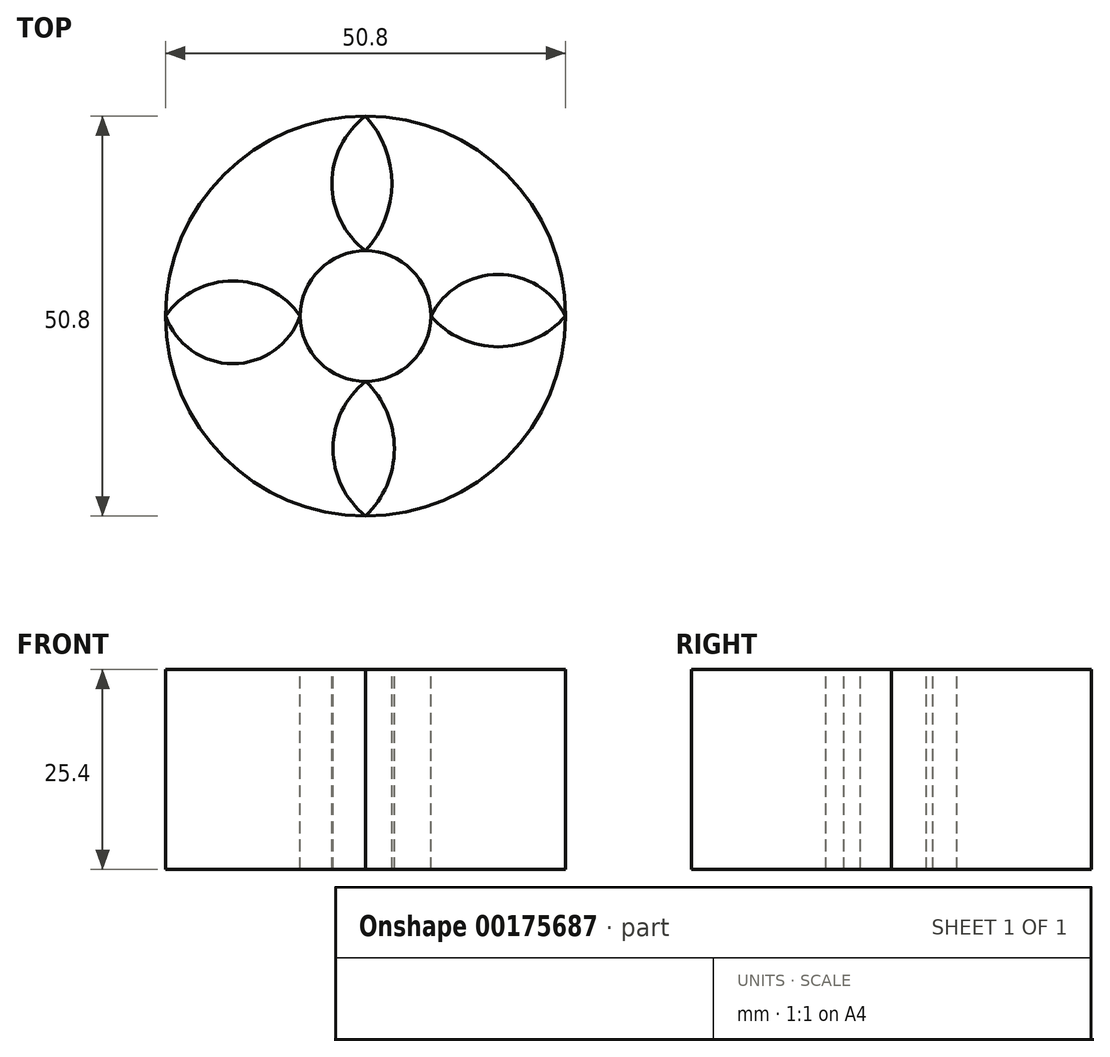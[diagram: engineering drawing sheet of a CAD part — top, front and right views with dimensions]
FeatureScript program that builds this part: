
annotation { "Feature Type Name" : "Feature", "Feature Type Description" : "" }
export const myFeature = defineFeature(function(context is Context, id is Id, definition is map)
    precondition{}
    {
        {
            var Q0;
            Q0=qCreatedBy(makeId("Top.planeOp"),FACE);
            var sketch = newSketch(context, id + "F0", { "sketchPlane" : qUnion([Q0])});
            skCircle(sketch, "E0", {"center": v(0, 0) * mm, "radius": 25.4 * mm});
            skSolve(sketch);
        }
        {
            var Q0;
            Q0 = qSketchRegion(id + "F0", true);
            extrude(context, id + "F1", {"entities" : qUnion([Q0]), "depth" : 25.4 * mm});
        }
        {
            var Q0;
            Q0=makeQuery(id+"F1.opExtrude","CAP_FACE",FACE,{"disambiguationData":[OSD([sQuery(id+"F0.wireOp",EDGE,"E0")])],"isStart":false});
            var sketch = newSketch(context, id + "F2", { "sketchPlane" : qUnion([Q0])});
            skCircle(sketch, "E1", {"center": v(0, 0) * mm, "radius": 8.3 * mm});
            skSolve(sketch);
        }
        {
            var Q0;
            Q0 = qSketchRegion(id + "F2", true);
            extrude(context, id + "F3", {"entities" : qUnion([Q0]), "operationType" : NewBodyOperationType.REMOVE, "endBound" : BoundingType.THROUGH_ALL, "oppositeDirection" : true, "depth" : 25.4 * mm});
        }
        {
            var Q0;
            Q0=makeQuery(id+"F1.opExtrude","CAP_FACE",FACE,{"disambiguationData":[OSD([sQuery(id+"F0.wireOp",EDGE,"E0")])],"isStart":false});
            var sketch = newSketch(context, id + "F4", { "sketchPlane" : qUnion([Q0])});
            skArc(sketch, "E2", {"start": v(0, 25.4) * mm, "mid": v(-4.27, 16.85) * mm, "end": v(0, 8.3) * mm});
            skArc(sketch, "E3", {"start": v(0, 8.3) * mm, "mid": v(3.34, 16.85) * mm, "end": v(0, 25.4) * mm});
            skArc(sketch, "E4", {"start": v(25.4, 0) * mm, "mid": v(16.85, 5.28) * mm, "end": v(8.3, 0) * mm});
            skArc(sketch, "E5", {"start": v(8.3, 0) * mm, "mid": v(16.85, -3.9) * mm, "end": v(25.4, 0) * mm});
            skArc(sketch, "E6", {"start": v(-25.4, 0) * mm, "mid": v(-16.85, -6.06) * mm, "end": v(-8.3, 0) * mm});
            skArc(sketch, "E7", {"start": v(-8.3, 0) * mm, "mid": v(-16.85, 4.46) * mm, "end": v(-25.4, 0) * mm});
            skArc(sketch, "E8", {"start": v(0, -25.4) * mm, "mid": v(3.66, -16.85) * mm, "end": v(0, -8.3) * mm});
            skArc(sketch, "E9", {"start": v(0, -8.3) * mm, "mid": v(-4.12, -16.85) * mm, "end": v(0, -25.4) * mm});
            skSolve(sketch);
        }
        {
            var Q0;
            Q0 = qSketchRegion(id + "F4", true);
            extrude(context, id + "F5", {"entities" : qUnion([Q0]), "operationType" : NewBodyOperationType.REMOVE, "endBound" : BoundingType.THROUGH_ALL, "oppositeDirection" : true, "depth" : 25.4 * mm});
        }
    });
